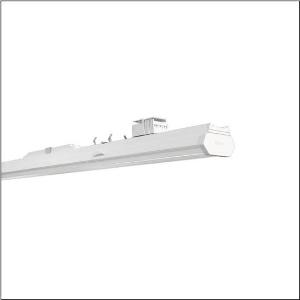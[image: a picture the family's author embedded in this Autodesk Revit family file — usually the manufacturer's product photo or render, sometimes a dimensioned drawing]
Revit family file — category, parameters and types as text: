
# Revit family: licross_r__11_protected_mo_51td117n485g_c933
name_source: partatom
category: Lighting Fixtures
units: mm (PartAtom-declared; Revit-internal decimal feet)

## family parameters
Cut with Voids When Loaded = No
Host = Face
Light Source = No
Part Type = Normal
Room Calculation Point = No
Round Connector Dimension = Use Diameter
Shared = No

## types (1)
- Licross® 11 Protected MO (1 x LED, 8680 lm, 48.6 W, 4000K)
    Apparent Load = 49 VA
    CIE Flux Codes = 83 94 98 100 100
    Color Rendering = 80
    Color Temperature = 4000K
    Default Elevation = 1800 mm
    Description = Licross® 11 Protected MO, luminaire insert, of sheet steel, galvanised, coil coated, white, length: 1.500mm, width: 90mm, height: 101mm, LED rated luminous flux: 8.680lm, light colour: 840, control gear: ON/OFF, with plug, 3-pole, with phase selection, mains connection: 220..240V, AC, 50/60Hz, rated input power: 49W, halogen-free wiring, primary light control with lens, of plastic, primary optical cover: cover, of PMMA, light emission: direct distribution, primary light characteristic: symmetric, protection rating (complete): IP54, insulation class (complete): insulation class I (protective earthing), certification: CE, ENEC, VDE, UKCA, protection symbol: D if used in an environment with non-conductive dust loads with corresponding accessories, impact resistance: IK06, permissible ambient temperature for indoor applications: -25..+35°C, corresponds to IFS (International Featured Standards) requirements for safety and quality in the food industry, reducing of maximum allowable ambient temperature of 5°C with ceiling mounting, LABS conformity tested according to VDMA 24364:2018-05, packaging unit: 1 piece
    Height = 92 mm
    Lamp = 1 x LED
    Lamp Light Flux = 8680 lm
    Lamp Power = 48.6 W
    Lamp count = 1
    Length = 1500 mm
    Luminous efficacy = 179 lm/W
    Manufacturer = Siteco
    ModVariant = No
    Model = 51TD117N485G
    Mounting Place = Ceiling
    Mounting Type = Pendant
    Number of Poles = 1
    OnlyDefault = Yes
    Power Factor = 1
    Product Name = Licross® 11 Protected MO
    Product group = luminaire insert
    ProductGroupID = 901
    Protection Class = Protection class I
    Protection Degree = IP 54
    RLX_Detail_Level = 1
    RLX_Emergency_Light_Flux = 0 lm
    RLX_Emergency_Type = 0
    RLX_Emergency_Type_DB = No
    RlxData = <blob elided: 20377 chars, md5=43c1f564>
    Socket = socket
    Standby Power = 0 W
    System Light Flux = 8680 lm
    System Power = 49 W
    Type Comments = Product without accessories
    Type Image = l_1256145.jpg
    URL = http://relux.com
    VarID = ---
    Voltage = 0 V
    Weight = 0.00 kg
    Width = 88 mm

## geometry (parser evidence)
native form markers: Blend x4, Sweep x11
no freeform markers — native parametric forms only
